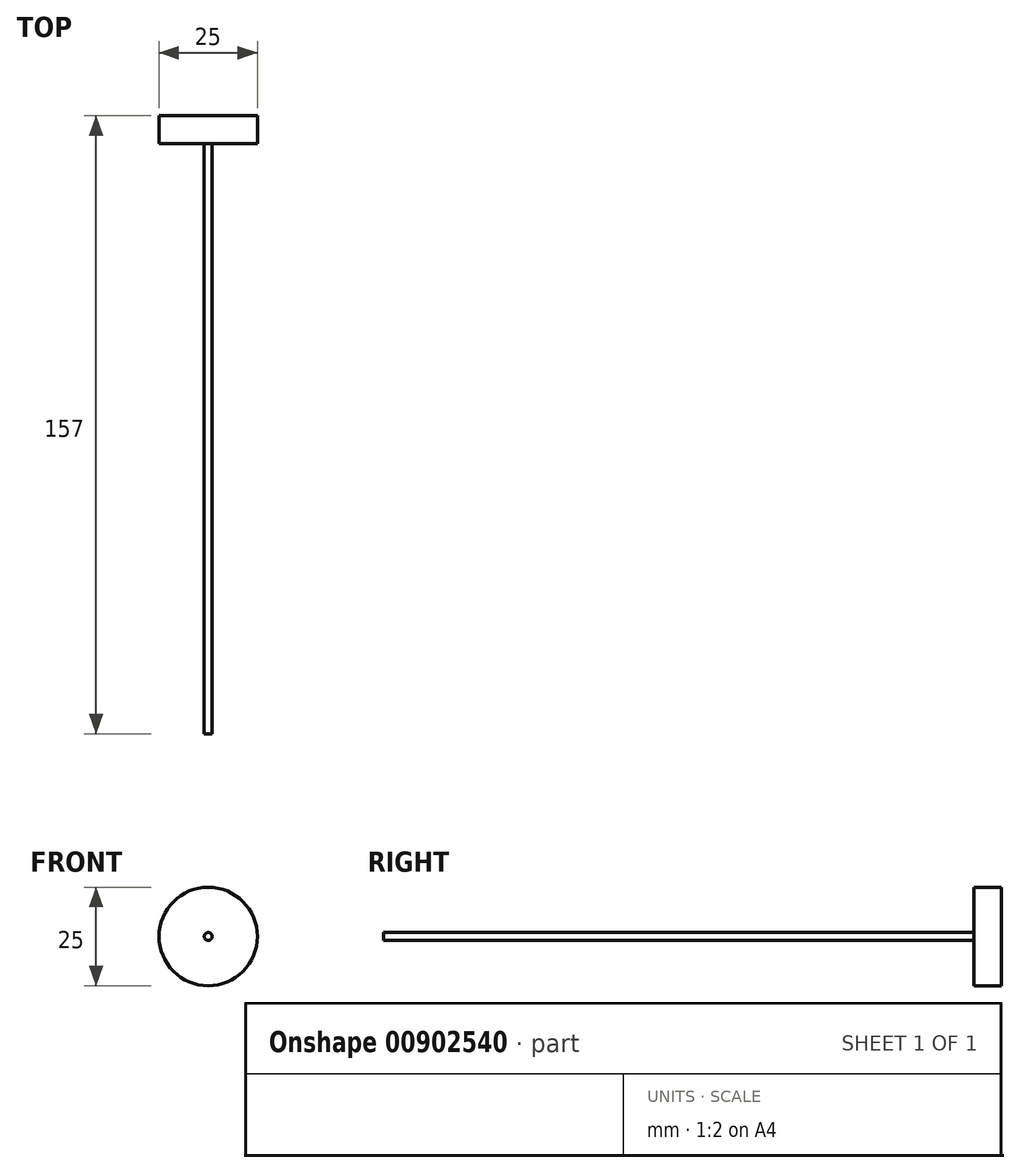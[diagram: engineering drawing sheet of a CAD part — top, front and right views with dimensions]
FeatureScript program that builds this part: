
annotation { "Feature Type Name" : "Feature", "Feature Type Description" : "" }
export const myFeature = defineFeature(function(context is Context, id is Id, definition is map)
    precondition{}
    {
        {
            var Q0;
            Q0=qCreatedBy(makeId("Front.planeOp"),FACE);
            var sketch = newSketch(context, id + "F0", { "sketchPlane" : qUnion([Q0])});
            skCircle(sketch, "E0", {"center": v(0, 0) * mm, "radius": 12.5 * mm});
            skCircle(sketch, "E1", {"center": v(0, 0) * mm, "radius": 1 * mm});
            skSolve(sketch);
        }
        {
            var Q0;
            Q0=makeQuery(id+"F0.imprint","IMPRINT",FACE,{"disambiguationData":[TD([[makeQuery(id+"F0.imprint","IMPRINT",EDGE,{"derivedFrom":sQuery(id+"F0.wireOp",EDGE,"E1")}),1.0]])]});
            extrude(context, id + "F1", {"entities" : qUnion([Q0]), "flatOperationType" : FlatOperationType.REMOVE, "depth" : 150 * mm, "offsetDistance" : 25 * mm, "domain" : OperationDomain.MODEL});
        }
        {
            var Q0;
            Q0=makeQuery(id+"F0.imprint","IMPRINT",FACE,{"disambiguationData":[TD([[makeQuery(id+"F0.imprint","IMPRINT",EDGE,{"derivedFrom":sQuery(id+"F0.wireOp",EDGE,"E0")}),1.0]])]});
            var Q1;
            Q1=makeQuery(id+"F0.imprint","IMPRINT",FACE,{"disambiguationData":[TD([[makeQuery(id+"F0.imprint","IMPRINT",EDGE,{"derivedFrom":sQuery(id+"F0.wireOp",EDGE,"E1")}),1.0]])]});
            extrude(context, id + "F2", {"entities" : qUnion([Q0, Q1]), "operationType" : NewBodyOperationType.ADD, "oppositeDirection" : true, "depth" : 7 * mm, "offsetDistance" : 25 * mm});
        }
    });
